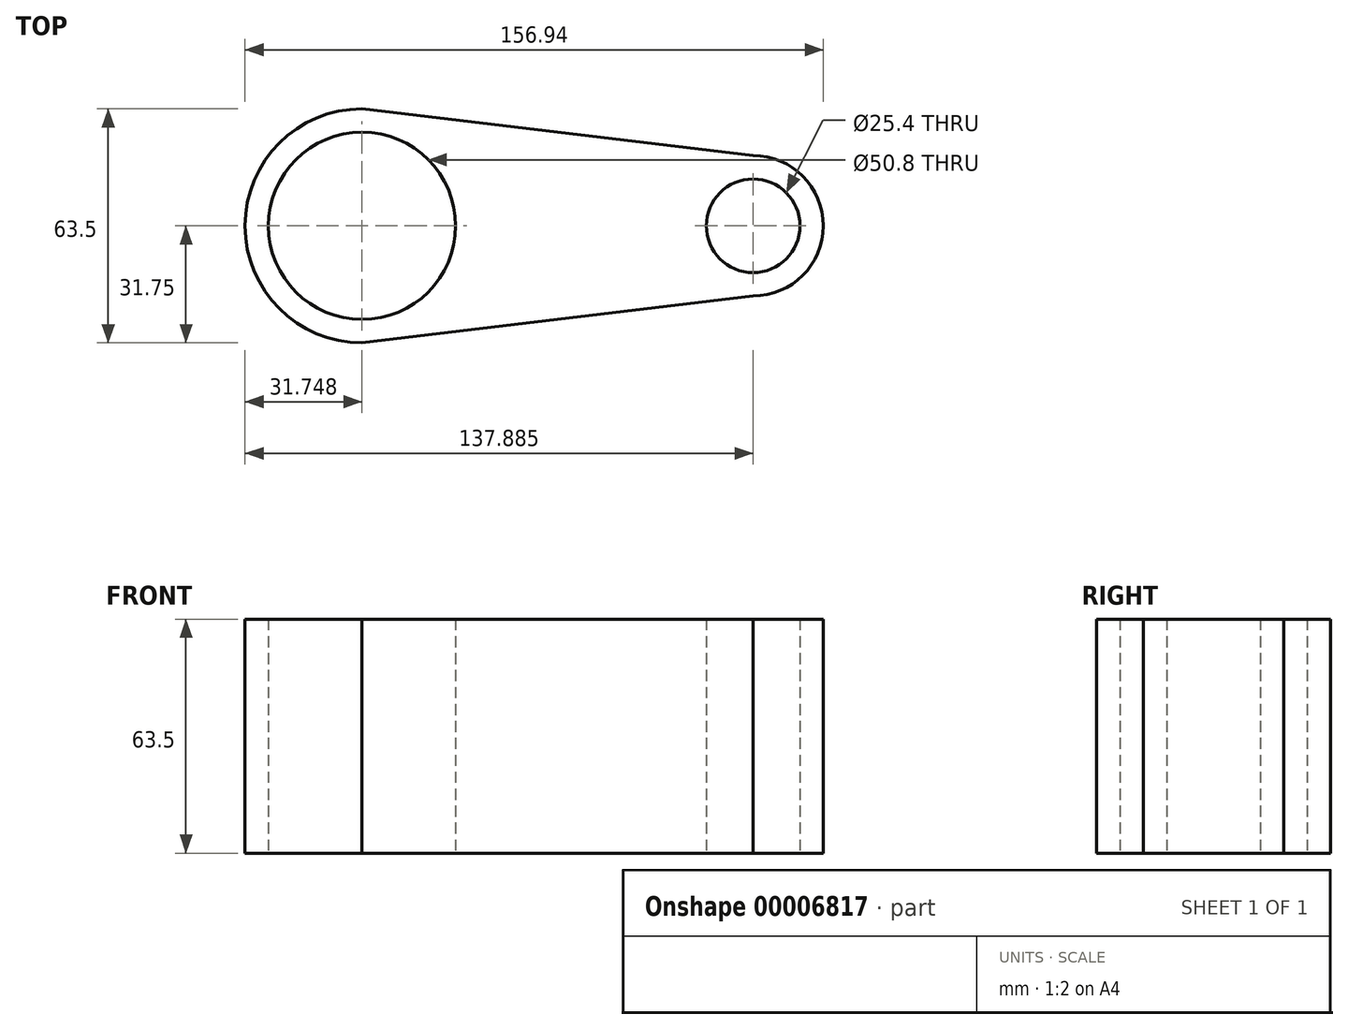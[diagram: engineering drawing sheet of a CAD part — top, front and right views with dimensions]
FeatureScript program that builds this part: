
annotation { "Feature Type Name" : "Feature", "Feature Type Description" : "" }
export const myFeature = defineFeature(function(context is Context, id is Id, definition is map)
    precondition{}
    {
        {
            var Q0;
            Q0=qCreatedBy(makeId("Top.planeOp"),FACE);
            var sketch = newSketch(context, id + "F0", { "sketchPlane" : qUnion([Q0])});
            skCircle(sketch, "E0", {"center": v(55.87, 0) * mm, "radius": 19.05 * mm});
            skCircle(sketch, "E1", {"center": v(-50.27, 0) * mm, "radius": 31.75 * mm});
            skLineSegment(sketch, "E2", {"start": v(55.87, -19.05) * mm, "end": v(-50.27, -31.75) * mm});
            skLineSegment(sketch, "E3", {"start": v(-50.27, 31.75) * mm, "end": v(55.87, 19.05) * mm});
            skCircle(sketch, "E4", {"center": v(-50.27, 0) * mm, "radius": 25.4 * mm});
            skCircle(sketch, "E5", {"center": v(55.87, 0) * mm, "radius": 12.7 * mm});
            skSolve(sketch);
        }
        {
            var Q0;
            {var subQ3=sQuery(id+"F0.wireOp",EDGE,"E0");var subQ5=sQuery(id+"F0.wireOp",EDGE,"E2");var subQ7=makeQuery(id+"F0.imprint","INTERSECT",VERTEX,{"derivedFrom":[subQ3,subQ5]});Q0=makeQuery(id+"F0.imprint","IMPRINT",FACE,{"disambiguationData":[TD([[makeQuery(id+"F0.imprint","IMPRINT",EDGE,{"disambiguationData":[TD([[subQ7,1.0]])],"derivedFrom":subQ3}),-1.0]])]});}
            var Q1;
            Q1=makeQuery(id+"F0.imprint","IMPRINT",FACE,{"disambiguationData":[TD([[makeQuery(id+"F0.imprint","IMPRINT",EDGE,{"derivedFrom":sQuery(id+"F0.wireOp",EDGE,"E4")}),-1.0]])]});
            var Q2;
            Q2=makeQuery(id+"F0.imprint","IMPRINT",FACE,{"disambiguationData":[TD([[makeQuery(id+"F0.imprint","IMPRINT",EDGE,{"derivedFrom":sQuery(id+"F0.wireOp",EDGE,"E5")}),-1.0]])]});
            extrude(context, id + "F1", {"entities" : qUnion([Q0, Q1, Q2]), "depth" : 63.5 * mm});
        }
    });
